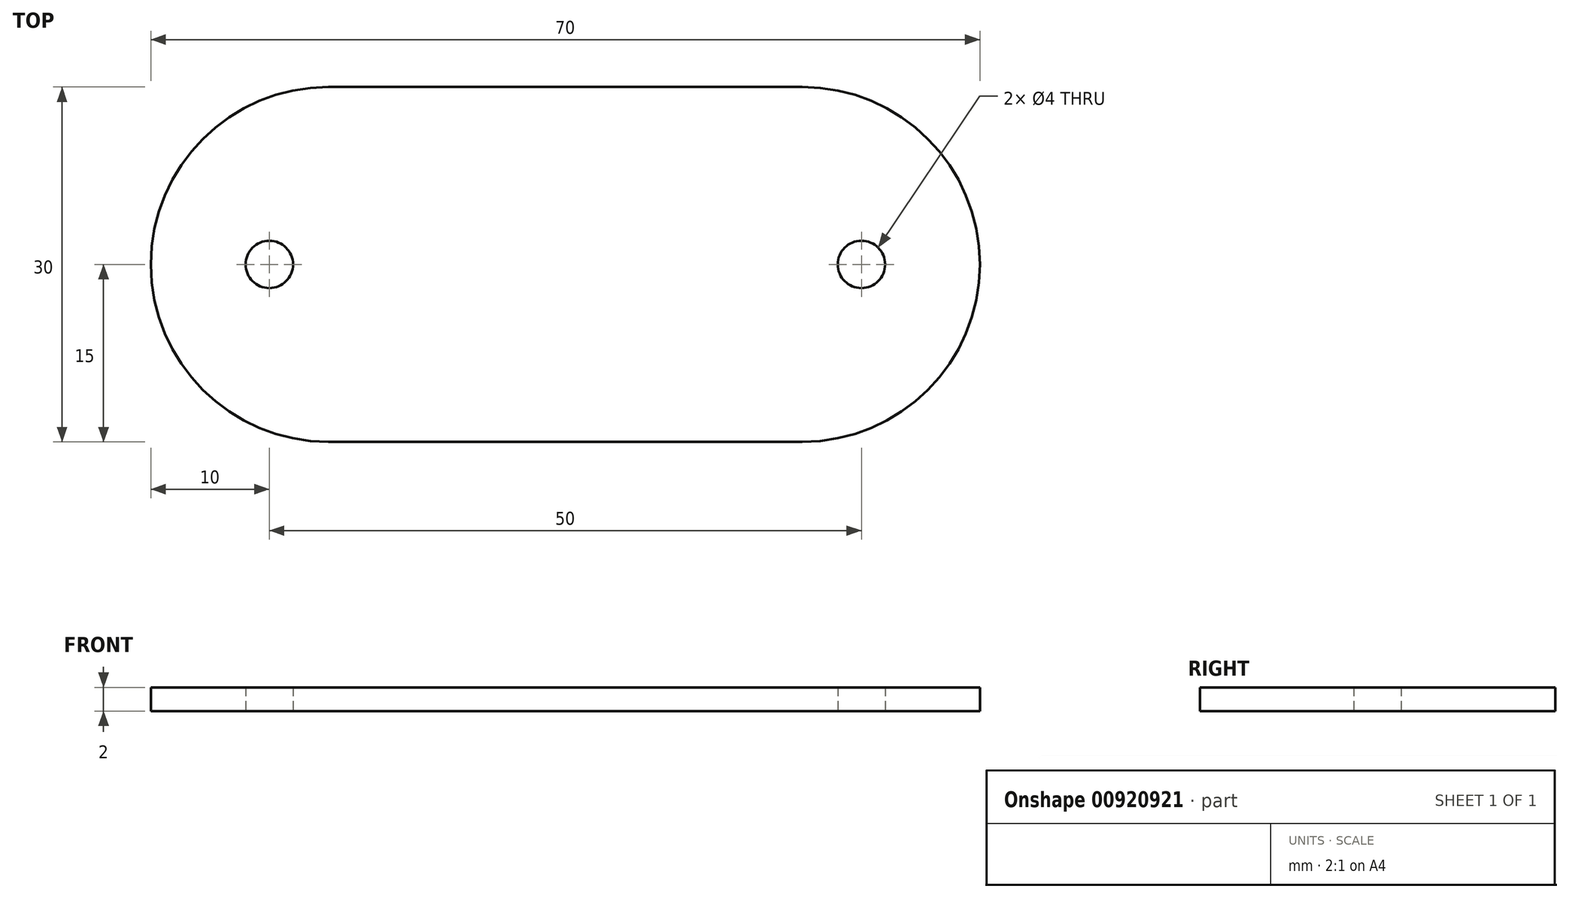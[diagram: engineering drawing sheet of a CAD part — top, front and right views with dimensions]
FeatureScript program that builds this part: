
annotation { "Feature Type Name" : "Feature", "Feature Type Description" : "" }
export const myFeature = defineFeature(function(context is Context, id is Id, definition is map)
    precondition{}
    {
        {
            var Q0;
            Q0=qCreatedBy(makeId("Top.planeOp"),FACE);
            var sketch = newSketch(context, id + "F0", { "sketchPlane" : qUnion([Q0])});
            skLineSegment(sketch, "E0", {"start": v(-20, 0) * mm, "end": v(20, 0) * mm});
            skArc(sketch, "E1.0.startCap", {"start": v(-20, -15) * mm, "mid": v(-35, 0) * mm, "end": v(-20, 15) * mm});
            skArc(sketch, "E1.0.endCap", {"start": v(20, 15) * mm, "mid": v(35, 0) * mm, "end": v(20, -15) * mm});
            skLineSegment(sketch, "E1.0.left", {"start": v(-20, 15) * mm, "end": v(20, 15) * mm});
            skLineSegment(sketch, "E1.0.right", {"start": v(-20, -15) * mm, "end": v(20, -15) * mm});
            skCircle(sketch, "E2", {"center": v(-25, 0) * mm, "radius": 2 * mm});
            skCircle(sketch, "E3", {"center": v(25, 0) * mm, "radius": 2 * mm});
            skPoint(sketch, "E4.center.orphan", {"position": v(0, 0) * mm});
            skSolve(sketch);
        }
        {
            var Q0;
            Q0=qSketchRegion(id+"F0",true);
            extrude(context, id + "F1", {"entities" : qUnion([Q0]), "depth" : 2 * mm, "offsetDistance" : 25 * mm});
        }
    });
